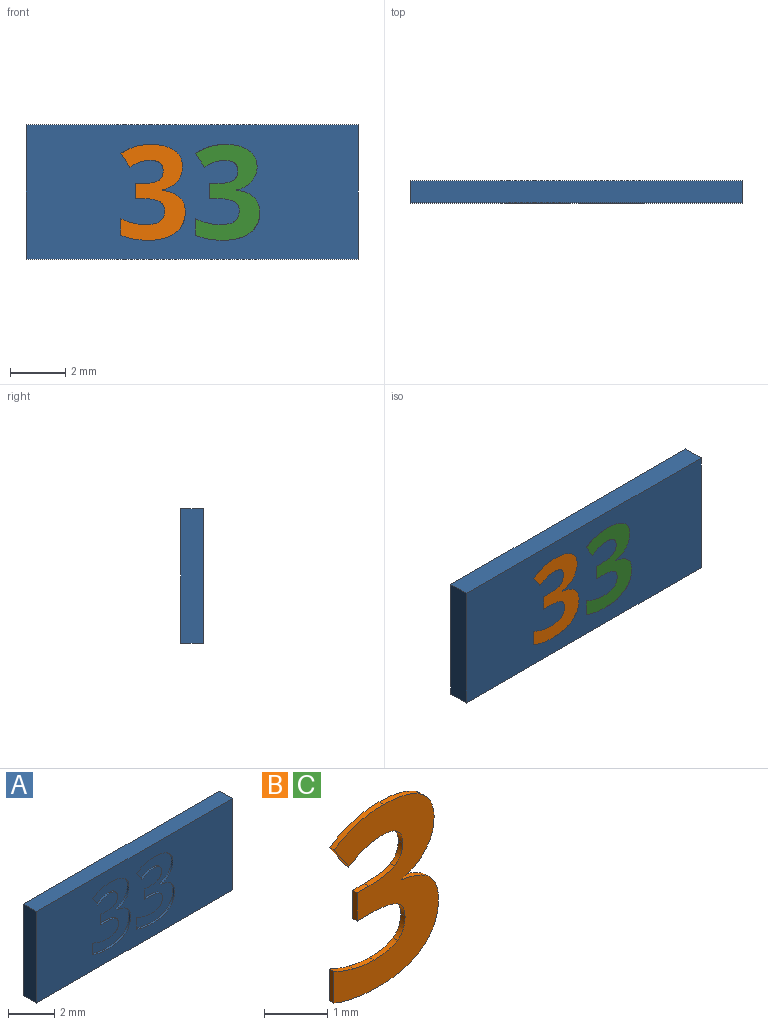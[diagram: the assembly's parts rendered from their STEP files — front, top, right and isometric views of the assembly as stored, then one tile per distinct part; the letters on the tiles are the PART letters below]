
ASSEMBLY  parts=3 mates=2
PART A: 62 faces, bbox 12x0.8x4.9 mm
  f0: plane 12x4.85mm, normal (0,-1,0), area 49.6mm2, adj f1,f2,f3,f4,f6,f7,f8,f9
  f1: plane 12x0.8mm, normal (0,0,-1), area 9.6mm2, adj f0,f2,f4,f5
  f2: plane 4.85x0.8mm, normal (1,0,0), area 3.9mm2, adj f0,f1,f3,f5
  f3: plane 12x0.8mm, normal (0,0,1), area 9.6mm2, adj f0,f2,f4,f5
  f4: plane 4.85x0.8mm, normal (-1,0,0), area 3.9mm2, adj f0,f1,f3,f5
  f5: plane 12x4.85mm, normal (0,1,0), area 58.2mm2, adj f1,f2,f3,f4
  f6: extruded ~0.59x0.3mm, area 0.1mm2, adj f0,f7,f32,f33
  f7: extruded ~0.83x0.21mm, area 0.1mm2, adj f0,f6,f8,f33
  f8: extruded ~1.1x0.33mm, area 0.1mm2, adj f0,f7,f9,f33
  f9: plane 0.49x0.33mm, normal (0.83,0,0.56), area 0.1mm2, adj f0,f8,f10,f33
  f10: extruded ~0.38x0.19mm, area 0mm2, adj f0,f9,f11,f33
  f11: extruded ~0.34x0.1mm, area 0mm2, adj f0,f10,f12,f33
  f12: extruded ~0.48x0.38mm, area 0.1mm2, adj f0,f11,f13,f33
  f13: extruded ~0.35x0.18mm, area 0mm2, adj f0,f12,f14,f33
  f14: extruded ~0.57x0.1mm, area 0.1mm2, adj f0,f13,f15,f33
  f15: plane 0.26x0.1mm, normal (0,0,-1), area 0mm2, adj f0,f14,f16,f33
  f16: plane 0.55x0.1mm, normal (1,0,0), area 0.1mm2, adj f0,f15,f17,f33
  f17: plane 0.26x0.1mm, normal (0,0,1), area 0mm2, adj f0,f16,f18,f33
  f18: extruded ~0.62x0.1mm, area 0.1mm2, adj f0,f17,f19,f33
  f19: extruded ~0.34x0.19mm, area 0mm2, adj f0,f18,f20,f33
  f20: extruded ~0.39x0.17mm, area 0mm2, adj f0,f19,f21,f33
  f21: extruded ~0.52x0.12mm, area 0.1mm2, adj f0,f20,f22,f33
  f22: extruded ~0.47x0.1mm, area 0mm2, adj f0,f21,f23,f33
  f23: extruded ~0.43x0.16mm, area 0mm2, adj f0,f22,f24,f33
  f24: plane 0.61x0.1mm, normal (1,0,0), area 0.1mm2, adj f0,f23,f25,f33
  f25: extruded ~0.97x0.18mm, area 0.1mm2, adj f0,f24,f26,f33
  f26: extruded ~1.01x0.27mm, area 0.1mm2, adj f0,f25,f27,f33
  f27: extruded ~0.76x0.35mm, area 0.1mm2, adj f0,f26,f28,f33
  f28: extruded ~0.53x0.21mm, area 0.1mm2, adj f0,f27,f29,f33
  f29: extruded ~0.62x0.25mm, area 0.1mm2, adj f0,f28,f30,f33
  f30: plane 0.1x0.01mm, normal (-1,0,0), area 0mm2, adj f0,f29,f31,f33
  f31: extruded ~0.54x0.3mm, area 0.1mm2, adj f0,f30,f32,f33
  f32: extruded ~0.54x0.19mm, area 0.1mm2, adj f0,f6,f31,f33
  f33: plane 3.47x2.33mm, normal (0,-1,0), area 4.3mm2, adj f6,f7,f8,f9,f10,f11,f12,f13
  f34: extruded ~0.59x0.3mm, area 0.1mm2, adj f0,f35,f60,f61
  f35: extruded ~0.83x0.21mm, area 0.1mm2, adj f0,f34,f36,f61
  f36: extruded ~1.1x0.33mm, area 0.1mm2, adj f0,f35,f37,f61
  f37: plane 0.49x0.33mm, normal (0.83,0,0.56), area 0.1mm2, adj f0,f36,f38,f61
  f38: extruded ~0.38x0.19mm, area 0mm2, adj f0,f37,f39,f61
  f39: extruded ~0.34x0.1mm, area 0mm2, adj f0,f38,f40,f61
  f40: extruded ~0.48x0.38mm, area 0.1mm2, adj f0,f39,f41,f61
  f41: extruded ~0.35x0.18mm, area 0mm2, adj f0,f40,f42,f61
  f42: extruded ~0.57x0.1mm, area 0.1mm2, adj f0,f41,f43,f61
  f43: plane 0.26x0.1mm, normal (0,0,-1), area 0mm2, adj f0,f42,f44,f61
  f44: plane 0.55x0.1mm, normal (1,0,0), area 0.1mm2, adj f0,f43,f45,f61
  f45: plane 0.26x0.1mm, normal (0,0,1), area 0mm2, adj f0,f44,f46,f61
  f46: extruded ~0.62x0.1mm, area 0.1mm2, adj f0,f45,f47,f61
  f47: extruded ~0.34x0.19mm, area 0mm2, adj f0,f46,f48,f61
  f48: extruded ~0.39x0.17mm, area 0mm2, adj f0,f47,f49,f61
  f49: extruded ~0.52x0.12mm, area 0.1mm2, adj f0,f48,f50,f61
  f50: extruded ~0.47x0.1mm, area 0mm2, adj f0,f49,f51,f61
  f51: extruded ~0.43x0.16mm, area 0mm2, adj f0,f50,f52,f61
  f52: plane 0.61x0.1mm, normal (1,0,0), area 0.1mm2, adj f0,f51,f53,f61
  f53: extruded ~0.97x0.18mm, area 0.1mm2, adj f0,f52,f54,f61
  f54: extruded ~1.01x0.27mm, area 0.1mm2, adj f0,f53,f55,f61
  f55: extruded ~0.76x0.35mm, area 0.1mm2, adj f0,f54,f56,f61
  f56: extruded ~0.53x0.21mm, area 0.1mm2, adj f0,f55,f57,f61
  f57: extruded ~0.62x0.25mm, area 0.1mm2, adj f0,f56,f58,f61
  f58: plane 0.1x0.01mm, normal (-1,0,0), area 0mm2, adj f0,f57,f59,f61
  f59: extruded ~0.54x0.3mm, area 0.1mm2, adj f0,f58,f60,f61
  f60: extruded ~0.54x0.19mm, area 0.1mm2, adj f0,f34,f59,f61
  f61: plane 3.47x2.33mm, normal (0,-1,0), area 4.3mm2, adj f34,f35,f36,f37,f38,f39,f40,f41
PART B: 29 faces, bbox 2.3x0.1x3.5 mm
  f0: plane 3.47x2.33mm, normal (0,-1,0), area 4.3mm2, adj f1,f2,f3,f4,f5,f6,f7,f8
  f1: extruded ~0.83x0.21mm, area 0.1mm2, adj f0,f2,f25,f27
  f2: extruded ~1.1x0.33mm, area 0.1mm2, adj f0,f1,f3,f25
  f3: plane 0.49x0.33mm, normal (-0.83,0,-0.56), area 0.1mm2, adj f0,f2,f4,f25
  f4: extruded ~0.38x0.19mm, area 0mm2, adj f0,f3,f5,f25
  f5: extruded ~0.34x0.1mm, area 0mm2, adj f0,f4,f6,f25
  f6: extruded ~0.48x0.38mm, area 0.1mm2, adj f0,f5,f7,f25
  f7: extruded ~0.35x0.18mm, area 0mm2, adj f0,f6,f8,f25
  f8: extruded ~0.57x0.1mm, area 0.1mm2, adj f0,f7,f9,f25
  f9: plane 0.26x0.1mm, normal (0,0,1), area 0mm2, adj f0,f8,f10,f25
  f10: plane 0.55x0.1mm, normal (-1,0,0), area 0.1mm2, adj f0,f9,f11,f25
  f11: plane 0.26x0.1mm, normal (0,0,-1), area 0mm2, adj f0,f10,f12,f25
  f12: extruded ~0.62x0.1mm, area 0.1mm2, adj f0,f11,f13,f25
  f13: extruded ~0.34x0.19mm, area 0mm2, adj f0,f12,f14,f25
  f14: extruded ~0.39x0.17mm, area 0mm2, adj f0,f13,f15,f25
  f15: extruded ~0.52x0.12mm, area 0.1mm2, adj f0,f14,f16,f25
  f16: extruded ~0.47x0.1mm, area 0mm2, adj f0,f15,f17,f25
  f17: extruded ~0.43x0.16mm, area 0mm2, adj f0,f16,f18,f25
  f18: plane 0.61x0.1mm, normal (-1,0,0), area 0.1mm2, adj f0,f17,f19,f25
  f19: extruded ~0.97x0.18mm, area 0.1mm2, adj f0,f18,f20,f25
  f20: extruded ~1.01x0.27mm, area 0.1mm2, adj f0,f19,f21,f25
  f21: extruded ~0.76x0.35mm, area 0.1mm2, adj f0,f20,f22,f25
  f22: extruded ~0.53x0.21mm, area 0.1mm2, adj f0,f21,f23,f25
  f23: extruded ~0.62x0.25mm, area 0.1mm2, adj f0,f22,f24,f25
  f24: plane 0.1x0.01mm, normal (1,0,0), area 0mm2, adj f0,f23,f25,f26
  f25: plane 3.47x2.33mm, normal (0,1,0), area 4.3mm2, adj f1,f2,f3,f4,f5,f6,f7,f8
  f26: extruded ~0.54x0.3mm, area 0.1mm2, adj f0,f24,f25,f28
  f27: extruded ~0.59x0.3mm, area 0.1mm2, adj f0,f1,f25,f28
  f28: extruded ~0.54x0.19mm, area 0.1mm2, adj f0,f25,f26,f27
PART C: same geometry as B
PLACE A t=(-0.02,0.37,-0.04)mm
PLACE B t=(-2.93,0.37,-0.04)mm
PLACE C t=(-0.24,0.37,-0.04)mm
MATE fastened B.f0 <-> A.f0  axis (0,-1,0) through (-2.59,-0.43,-1.6)mm
MATE fastened C.f0 <-> A.f0  axis (0,-1,0) through (0.1,-0.43,-1.6)mm
